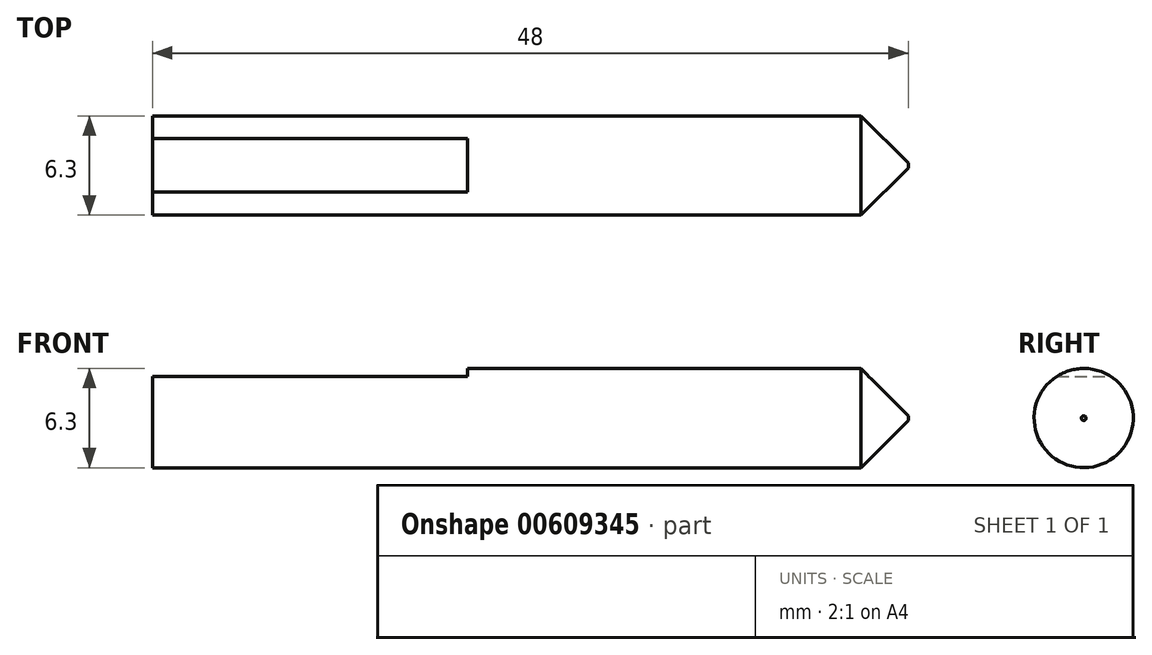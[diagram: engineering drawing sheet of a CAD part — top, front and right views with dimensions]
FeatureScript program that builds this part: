
annotation { "Feature Type Name" : "Feature", "Feature Type Description" : "" }
export const myFeature = defineFeature(function(context is Context, id is Id, definition is map)
    precondition{}
    {
        {
            var Q0;
            Q0=qCreatedBy(makeId("Front.planeOp"),FACE);
            var sketch = newSketch(context, id + "F0", { "sketchPlane" : qUnion([Q0])});
            skLineSegment(sketch, "E0", {"start": v(0, 3.15) * mm, "end": v(48, 3.15) * mm});
            skLineSegment(sketch, "E1", {"start": v(48, 0) * mm, "end": v(0, 0) * mm});
            skLineSegment(sketch, "E2", {"start": v(0, 0) * mm, "end": v(0, 3.15) * mm});
            skLineSegment(sketch, "E3", {"start": v(48, 3.15) * mm, "end": v(48, 0) * mm});
            skSolve(sketch);
        }
        {
            var Q0;
            Q0=makeQuery(id+"F0.imprint","IMPRINT",FACE,{"disambiguationData":[TD([[makeQuery(id+"F0.imprint","IMPRINT",EDGE,{"derivedFrom":sQuery(id+"F0.wireOp",EDGE,"E0")}),-1.0]])]});
            var Q1;
            Q1=sQuery(id+"F0.wireOp",EDGE,"E1");
            revolve(context, id + "F1", {"entities" : qUnion([Q0]), "axis" : qUnion([Q1]), "revolveType" : RevolveType.FULL});
        }
        {
            var Q0;
            Q0=makeQuery(id+"F1.opRevolve","SWEPT_EDGE",EDGE,{"disambiguationData":[OSD([sQuery(id+"F0.wireOp",EDGE,"E0"),sQuery(id+"F0.wireOp",EDGE,"E3")])]});
            chamfer(context, id + "F2", {"entities" : qUnion([Q0]), "width" : 3 * mm, "tangentPropagation" : true});
        }
        {
            var Q0;
            Q0=makeQuery(id+"F1.opRevolve","SWEPT_FACE",FACE,{"disambiguationData":[OSD([sQuery(id+"F0.wireOp",EDGE,"E2")])]});
            var sketch = newSketch(context, id + "F3", { "sketchPlane" : qUnion([Q0])});
            skLineSegment(sketch, "E4.bottom", {"start": v(1.7, 2.65) * mm, "end": v(-1.7, 2.65) * mm});
            skLineSegment(sketch, "E4.top", {"start": v(1.7, 3.15) * mm, "end": v(-1.7, 3.15) * mm});
            skLineSegment(sketch, "E4.left", {"start": v(1.7, 2.65) * mm, "end": v(1.7, 3.15) * mm});
            skLineSegment(sketch, "E4.right", {"start": v(-1.7, 2.65) * mm, "end": v(-1.7, 3.15) * mm});
            skPoint(sketch, "E4.middle", {"position": v(0, 2.9) * mm});
            skSolve(sketch);
        }
        {
            var Q0;
            {var subQ0=sQuery(id+"F3.wireOp",EDGE,"E4.bottom");Q0=makeQuery(id+"F3.imprint","IMPRINT",FACE,{"disambiguationData":[TD([[makeQuery(id+"F3.imprint","IMPRINT",EDGE,{"derivedFrom":subQ0}),-1.0]])]});}
            extrude(context, id + "F4", {"entities" : qUnion([Q0]), "operationType" : NewBodyOperationType.REMOVE, "oppositeDirection" : true, "depth" : 20 * mm, "offsetDistance" : 25 * mm});
        }
    });
